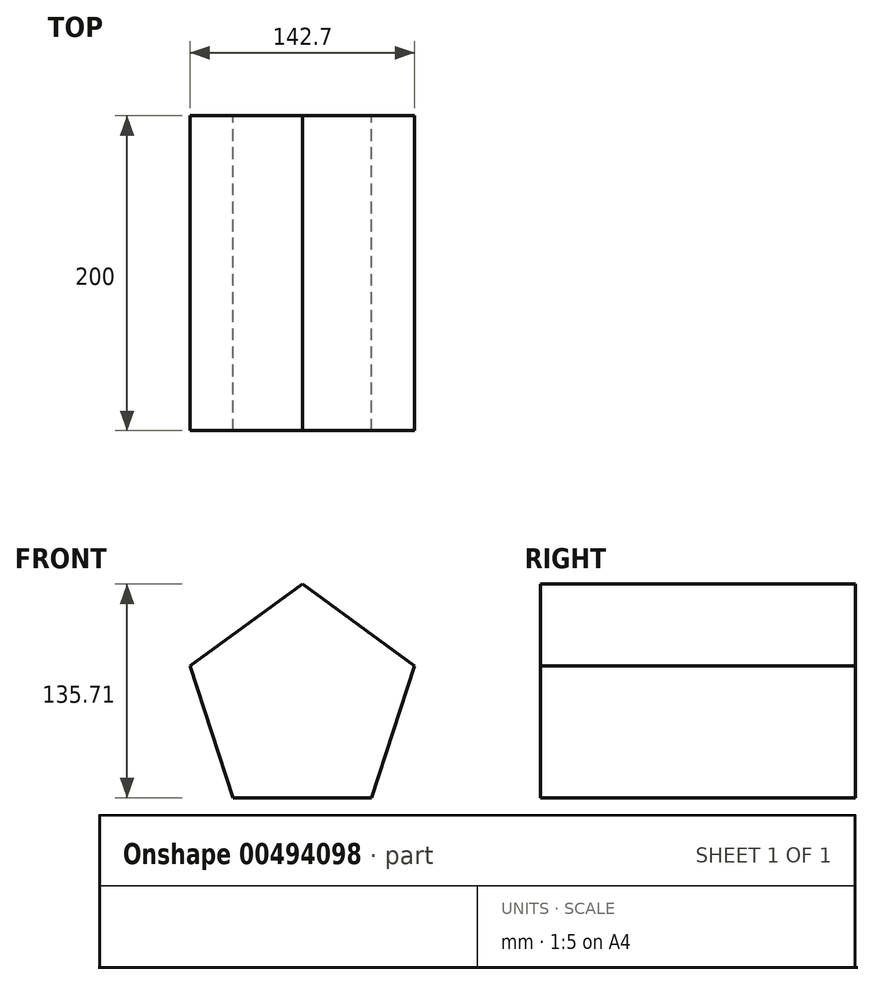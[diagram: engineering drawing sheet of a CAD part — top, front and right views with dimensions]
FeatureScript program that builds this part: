
annotation { "Feature Type Name" : "Feature", "Feature Type Description" : "" }
export const myFeature = defineFeature(function(context is Context, id is Id, definition is map)
    precondition{}
    {
        {
            var Q0;
            Q0=qCreatedBy(makeId("Front.planeOp"),FACE);
            var sketch = newSketch(context, id + "F0", { "sketchPlane" : qUnion([Q0])});
            skCircle(sketch, "E0.cCircle", {"center": v(0, 0) * mm, "radius": 75.02 * mm, "construction": true});
            skLineSegment(sketch, "E0.0", {"start": v(0, 75.02) * mm, "end": v(71.35, 23.18) * mm});
            skLineSegment(sketch, "E0.1", {"start": v(71.35, 23.18) * mm, "end": v(44.1, -60.7) * mm});
            skLineSegment(sketch, "E0.2", {"start": v(44.1, -60.7) * mm, "end": v(-44.1, -60.7) * mm});
            skLineSegment(sketch, "E0.3", {"start": v(-44.1, -60.7) * mm, "end": v(-71.35, 23.18) * mm});
            skLineSegment(sketch, "E0.4", {"start": v(-71.35, 23.18) * mm, "end": v(0, 75.02) * mm});
            skSolve(sketch);
        }
        {
            var Q0;
            Q0 = qSketchRegion(id + "F0", true);
            extrude(context, id + "F1", {"entities" : qUnion([Q0]), "depth" : 200 * mm});
        }
    });
